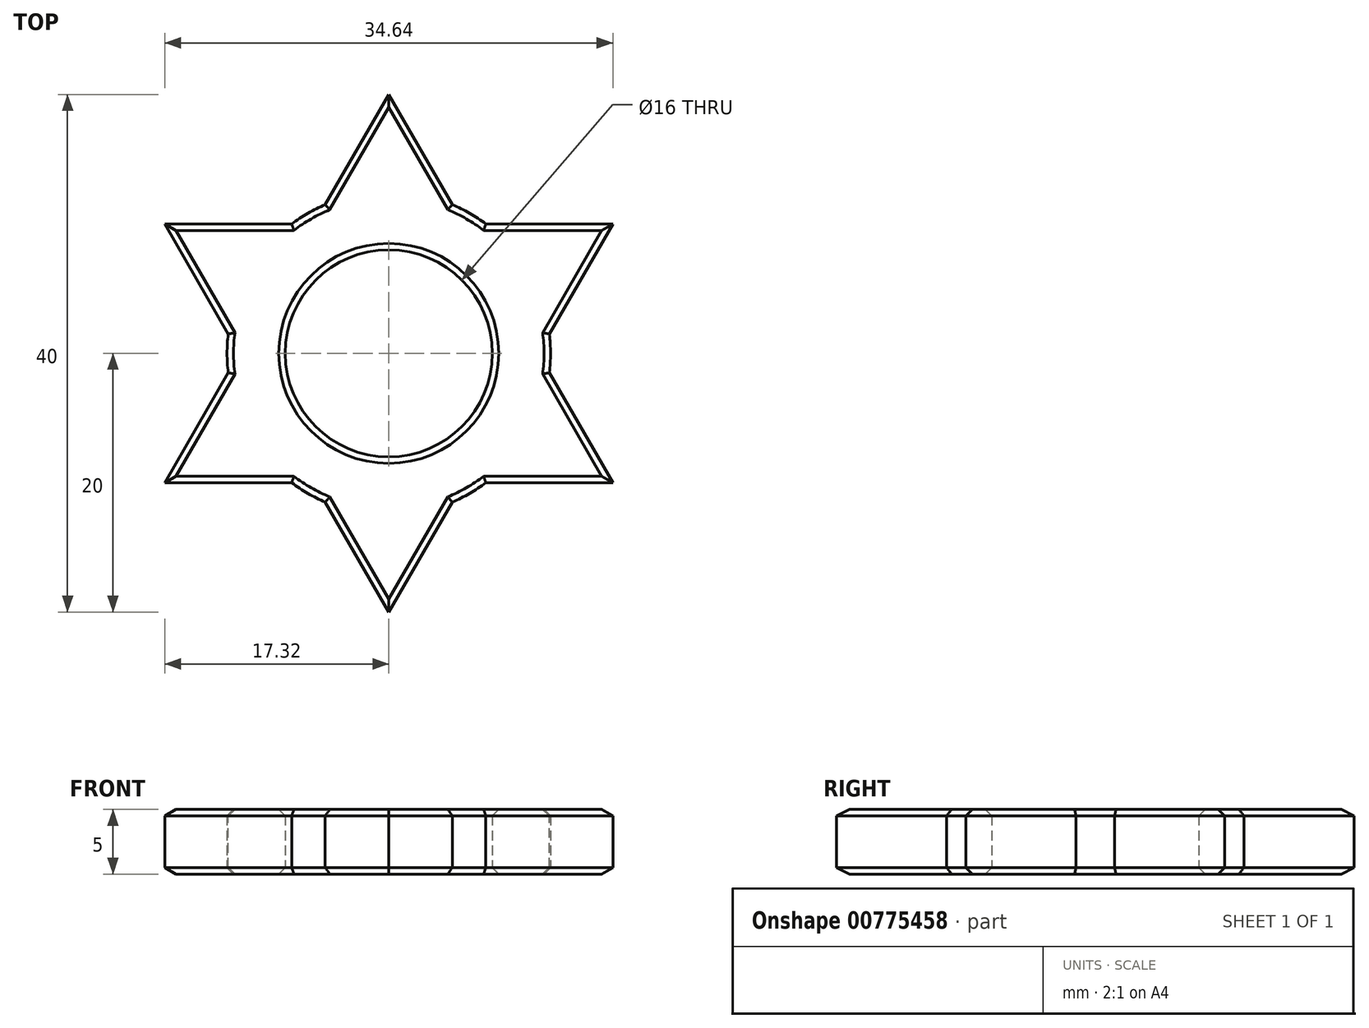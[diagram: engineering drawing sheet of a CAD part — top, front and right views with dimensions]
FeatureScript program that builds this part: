
annotation { "Feature Type Name" : "Feature", "Feature Type Description" : "" }
export const myFeature = defineFeature(function(context is Context, id is Id, definition is map)
    precondition{}
    {
        {
            var Q0;
            Q0=qCreatedBy(makeId("Top.planeOp"),FACE);
            var sketch = newSketch(context, id + "F0", { "sketchPlane" : qUnion([Q0])});
            skCircle(sketch, "E0", {"center": v(0, 0) * mm, "radius": 12.5 * mm});
            skCircle(sketch, "E1", {"center": v(0, 0) * mm, "radius": 8 * mm});
            skSolve(sketch);
        }
        {
            var Q0;
            Q0=qSketchRegion(id+"F0",true);
            extrude(context, id + "F1", {"entities" : qUnion([Q0]), "endBound" : BoundingType.SYMMETRIC, "depth" : 5 * mm, "offsetDistance" : 25.4 * mm});
        }
        {
            var Q0;
            Q0=makeQuery(id+"F1.opExtrude","CAP_FACE",FACE,{"disambiguationData":[OSD([sQuery(id+"F0.wireOp",EDGE,"E0"),sQuery(id+"F0.wireOp",EDGE,"E1")])],"isStart":false});
            var sketch = newSketch(context, id + "F2", { "sketchPlane" : qUnion([Q0])});
            skLineSegment(sketch, "E2", {"start": v(0, 0) * mm, "end": v(0, 20) * mm});
            skCircle(sketch, "E3.0", {"center": v(0, 0) * mm, "radius": 12.5 * mm});
            skLineSegment(sketch, "E4", {"start": v(0, 20) * mm, "end": v(-4.91, 11.5) * mm});
            skLineSegment(sketch, "E5", {"start": v(0, 20) * mm, "end": v(4.91, 11.5) * mm});
            skLineSegment(sketch, "E6.1.0", {"start": v(-17.32, 10) * mm, "end": v(-12.41, 1.5) * mm});
            skLineSegment(sketch, "E6.1.1", {"start": v(-17.32, 10) * mm, "end": v(-7.5, 10) * mm});
            skLineSegment(sketch, "E6.2.0", {"start": v(-17.32, -10) * mm, "end": v(-7.5, -10) * mm});
            skLineSegment(sketch, "E6.2.1", {"start": v(-17.32, -10) * mm, "end": v(-12.41, -1.5) * mm});
            skLineSegment(sketch, "E6.3.0", {"start": v(0, -20) * mm, "end": v(4.91, -11.5) * mm});
            skLineSegment(sketch, "E6.3.1", {"start": v(0, -20) * mm, "end": v(-4.91, -11.5) * mm});
            skLineSegment(sketch, "E6.4.0", {"start": v(17.32, -10) * mm, "end": v(12.41, -1.5) * mm});
            skLineSegment(sketch, "E6.4.1", {"start": v(17.32, -10) * mm, "end": v(7.5, -10) * mm});
            skLineSegment(sketch, "E6.5.0", {"start": v(17.32, 10) * mm, "end": v(7.5, 10) * mm});
            skLineSegment(sketch, "E6.5.1", {"start": v(17.32, 10) * mm, "end": v(12.41, 1.5) * mm});
            skSolve(sketch);
        }
        {
            var Q0;
            {var subQ0=sQuery(id+"F2.wireOp",EDGE,"E4");Q0=makeQuery(id+"F2.imprint","IMPRINT",FACE,{"disambiguationData":[TD([[makeQuery(id+"F2.imprint","IMPRINT",EDGE,{"derivedFrom":subQ0}),1.0]])]});}
            var Q1;
            {var subQ0=sQuery(id+"F2.wireOp",EDGE,"E5");Q1=makeQuery(id+"F2.imprint","IMPRINT",FACE,{"disambiguationData":[TD([[makeQuery(id+"F2.imprint","IMPRINT",EDGE,{"derivedFrom":subQ0}),-1.0]])]});}
            var Q2;
            {var subQ0=sQuery(id+"F2.wireOp",EDGE,"E6.5.0");Q2=makeQuery(id+"F2.imprint","IMPRINT",FACE,{"disambiguationData":[TD([[makeQuery(id+"F2.imprint","IMPRINT",EDGE,{"derivedFrom":subQ0}),1.0]])]});}
            var Q3;
            {var subQ0=sQuery(id+"F2.wireOp",EDGE,"E6.1.0");Q3=makeQuery(id+"F2.imprint","IMPRINT",FACE,{"disambiguationData":[TD([[makeQuery(id+"F2.imprint","IMPRINT",EDGE,{"derivedFrom":subQ0}),1.0]])]});}
            var Q4;
            {var subQ0=sQuery(id+"F2.wireOp",EDGE,"E6.2.0");Q4=makeQuery(id+"F2.imprint","IMPRINT",FACE,{"disambiguationData":[TD([[makeQuery(id+"F2.imprint","IMPRINT",EDGE,{"derivedFrom":subQ0}),1.0]])]});}
            var Q5;
            {var subQ0=sQuery(id+"F2.wireOp",EDGE,"E6.4.0");Q5=makeQuery(id+"F2.imprint","IMPRINT",FACE,{"disambiguationData":[TD([[makeQuery(id+"F2.imprint","IMPRINT",EDGE,{"derivedFrom":subQ0}),1.0]])]});}
            var Q6;
            {var subQ0=sQuery(id+"F2.wireOp",EDGE,"E6.3.0");Q6=makeQuery(id+"F2.imprint","IMPRINT",FACE,{"disambiguationData":[TD([[makeQuery(id+"F2.imprint","IMPRINT",EDGE,{"derivedFrom":subQ0}),1.0]])]});}
            extrude(context, id + "F3", {"entities" : qUnion([Q0, Q1, Q2, Q3, Q4, Q5, Q6]), "operationType" : NewBodyOperationType.ADD, "oppositeDirection" : true, "depth" : 5 * mm, "offsetDistance" : 25.4 * mm});
        }
        {
            var Q0;
            {var subQ0=sQuery(id+"F2.wireOp",EDGE,"E3.0");Q0=makeQuery(id+"F3.boolean.opBoolean","MERGE",FACE,{"derivedFrom":[makeQuery(id+"F1.opExtrude","CAP_FACE",FACE,{"disambiguationData":[OSD([sQuery(id+"F0.wireOp",EDGE,"E0"),sQuery(id+"F0.wireOp",EDGE,"E1")])],"isStart":false}),makeQuery(id+"F3.opExtrude","CAP_FACE",FACE,{"disambiguationData":[OSD([subQ0,sQuery(id+"F2.wireOp",EDGE,"E6.5.0"),sQuery(id+"F2.wireOp",EDGE,"E6.5.1")])],"isStart":true}),makeQuery(id+"F3.opExtrude","CAP_FACE",FACE,{"disambiguationData":[OSD([subQ0,sQuery(id+"F2.wireOp",EDGE,"E4"),sQuery(id+"F2.wireOp",EDGE,"E5")])],"isStart":true}),makeQuery(id+"F3.opExtrude","CAP_FACE",FACE,{"disambiguationData":[OSD([subQ0,sQuery(id+"F2.wireOp",EDGE,"E6.1.0"),sQuery(id+"F2.wireOp",EDGE,"E6.1.1")])],"isStart":true}),makeQuery(id+"F3.opExtrude","CAP_FACE",FACE,{"disambiguationData":[OSD([subQ0,sQuery(id+"F2.wireOp",EDGE,"E6.2.0"),sQuery(id+"F2.wireOp",EDGE,"E6.2.1")])],"isStart":true}),makeQuery(id+"F3.opExtrude","CAP_FACE",FACE,{"disambiguationData":[OSD([subQ0,sQuery(id+"F2.wireOp",EDGE,"E6.3.0"),sQuery(id+"F2.wireOp",EDGE,"E6.3.1")])],"isStart":true}),makeQuery(id+"F3.opExtrude","CAP_FACE",FACE,{"disambiguationData":[OSD([subQ0,sQuery(id+"F2.wireOp",EDGE,"E6.4.0"),sQuery(id+"F2.wireOp",EDGE,"E6.4.1")])],"isStart":true})]});}
            var Q1;
            {var subQ0=sQuery(id+"F2.wireOp",EDGE,"E3.0");Q1=makeQuery(id+"F3.boolean.opBoolean","MERGE",FACE,{"derivedFrom":[makeQuery(id+"F1.opExtrude","CAP_FACE",FACE,{"disambiguationData":[OSD([sQuery(id+"F0.wireOp",EDGE,"E0"),sQuery(id+"F0.wireOp",EDGE,"E1")])],"isStart":true}),makeQuery(id+"F3.opExtrude","CAP_FACE",FACE,{"disambiguationData":[OSD([subQ0,sQuery(id+"F2.wireOp",EDGE,"E6.5.0"),sQuery(id+"F2.wireOp",EDGE,"E6.5.1")])],"isStart":false}),makeQuery(id+"F3.opExtrude","CAP_FACE",FACE,{"disambiguationData":[OSD([subQ0,sQuery(id+"F2.wireOp",EDGE,"E4"),sQuery(id+"F2.wireOp",EDGE,"E5")])],"isStart":false}),makeQuery(id+"F3.opExtrude","CAP_FACE",FACE,{"disambiguationData":[OSD([subQ0,sQuery(id+"F2.wireOp",EDGE,"E6.1.0"),sQuery(id+"F2.wireOp",EDGE,"E6.1.1")])],"isStart":false}),makeQuery(id+"F3.opExtrude","CAP_FACE",FACE,{"disambiguationData":[OSD([subQ0,sQuery(id+"F2.wireOp",EDGE,"E6.2.0"),sQuery(id+"F2.wireOp",EDGE,"E6.2.1")])],"isStart":false}),makeQuery(id+"F3.opExtrude","CAP_FACE",FACE,{"disambiguationData":[OSD([subQ0,sQuery(id+"F2.wireOp",EDGE,"E6.3.0"),sQuery(id+"F2.wireOp",EDGE,"E6.3.1")])],"isStart":false}),makeQuery(id+"F3.opExtrude","CAP_FACE",FACE,{"disambiguationData":[OSD([subQ0,sQuery(id+"F2.wireOp",EDGE,"E6.4.0"),sQuery(id+"F2.wireOp",EDGE,"E6.4.1")])],"isStart":false})]});}
            chamfer(context, id + "F4", {"entities" : qUnion([Q0, Q1]), "width" : .5 * mm, "tangentPropagation" : true});
        }
    });
